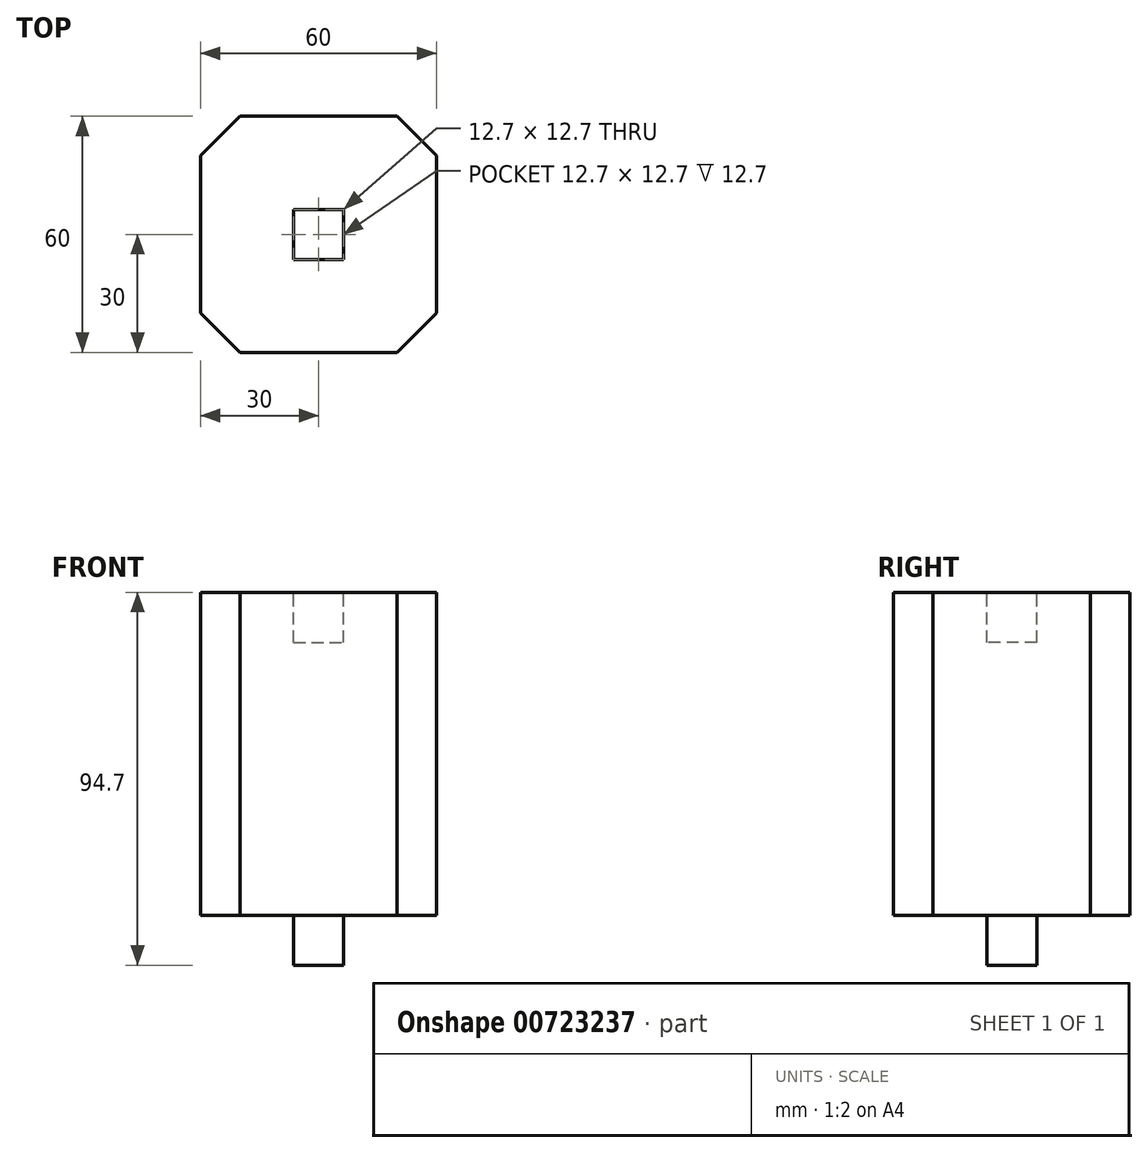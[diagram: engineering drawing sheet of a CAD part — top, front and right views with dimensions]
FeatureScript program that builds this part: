
annotation { "Feature Type Name" : "Feature", "Feature Type Description" : "" }
export const myFeature = defineFeature(function(context is Context, id is Id, definition is map)
    precondition{}
    {
        {
            var Q0;
            Q0=qCreatedBy(makeId("Top.planeOp"),FACE);
            var sketch = newSketch(context, id + "F0", { "sketchPlane" : qUnion([Q0])});
            skLineSegment(sketch, "E0.bottom", {"start": v(-30, 30) * mm, "end": v(30, 30) * mm});
            skLineSegment(sketch, "E0.top", {"start": v(-30, -30) * mm, "end": v(30, -30) * mm});
            skLineSegment(sketch, "E0.left", {"start": v(-30, 30) * mm, "end": v(-30, -30) * mm});
            skLineSegment(sketch, "E0.right", {"start": v(30, 30) * mm, "end": v(30, -30) * mm});
            skSolve(sketch);
        }
        {
            var Q0;
            Q0=qSketchRegion(id+"F0",true);
            extrude(context, id + "F1", {"entities" : qUnion([Q0]), "depth" : 82 * mm, "offsetDistance" : 25 * mm});
        }
        {
            var Q0;
            Q0=makeQuery(id+"F1.opExtrude","SWEPT_EDGE",EDGE,{"disambiguationData":[OSD([sQuery(id+"F0.wireOp",EDGE,"E0.top"),sQuery(id+"F0.wireOp",EDGE,"E0.right")])]});
            var Q1;
            Q1=makeQuery(id+"F1.opExtrude","SWEPT_EDGE",EDGE,{"disambiguationData":[OSD([sQuery(id+"F0.wireOp",EDGE,"E0.bottom"),sQuery(id+"F0.wireOp",EDGE,"E0.right")])]});
            var Q2;
            Q2=makeQuery(id+"F1.opExtrude","SWEPT_EDGE",EDGE,{"disambiguationData":[OSD([sQuery(id+"F0.wireOp",EDGE,"E0.top"),sQuery(id+"F0.wireOp",EDGE,"E0.left")])]});
            var Q3;
            Q3=makeQuery(id+"F1.opExtrude","SWEPT_EDGE",EDGE,{"disambiguationData":[OSD([sQuery(id+"F0.wireOp",EDGE,"E0.bottom"),sQuery(id+"F0.wireOp",EDGE,"E0.left")])]});
            chamfer(context, id + "F2", {"entities" : qUnion([Q0, Q1, Q2, Q3]), "width" : 10 * mm, "tangentPropagation" : true});
        }
        {
            var Q0;
            Q0=makeQuery(id+"F1.opExtrude","CAP_FACE",FACE,{"disambiguationData":[OSD([sQuery(id+"F0.wireOp",EDGE,"E0.bottom"),sQuery(id+"F0.wireOp",EDGE,"E0.top"),sQuery(id+"F0.wireOp",EDGE,"E0.left"),sQuery(id+"F0.wireOp",EDGE,"E0.right")])],"isStart":false});
            var sketch = newSketch(context, id + "F3", { "sketchPlane" : qUnion([Q0])});
            skLineSegment(sketch, "E1.bottom", {"start": v(-6.35, 6.35) * mm, "end": v(6.35, 6.35) * mm});
            skLineSegment(sketch, "E1.top", {"start": v(-6.35, -6.35) * mm, "end": v(6.35, -6.35) * mm});
            skLineSegment(sketch, "E1.left", {"start": v(-6.35, 6.35) * mm, "end": v(-6.35, -6.35) * mm});
            skLineSegment(sketch, "E1.right", {"start": v(6.35, 6.35) * mm, "end": v(6.35, -6.35) * mm});
            skSolve(sketch);
        }
        {
            var Q0;
            Q0=qSketchRegion(id+"F3",true);
            extrude(context, id + "F4", {"entities" : qUnion([Q0]), "operationType" : NewBodyOperationType.REMOVE, "oppositeDirection" : true, "depth" : 12.7 * mm, "offsetDistance" : 25 * mm});
        }
        {
            var Q0;
            Q0=makeQuery(id+"F1.opExtrude","CAP_FACE",FACE,{"disambiguationData":[OSD([sQuery(id+"F0.wireOp",EDGE,"E0.bottom"),sQuery(id+"F0.wireOp",EDGE,"E0.top"),sQuery(id+"F0.wireOp",EDGE,"E0.left"),sQuery(id+"F0.wireOp",EDGE,"E0.right")])],"isStart":true});
            var sketch = newSketch(context, id + "F5", { "sketchPlane" : qUnion([Q0])});
            skLineSegment(sketch, "E2.bottom", {"start": v(-6.35, 6.35) * mm, "end": v(6.35, 6.35) * mm});
            skLineSegment(sketch, "E2.top", {"start": v(-6.35, -6.35) * mm, "end": v(6.35, -6.35) * mm});
            skLineSegment(sketch, "E2.left", {"start": v(-6.35, 6.35) * mm, "end": v(-6.35, -6.35) * mm});
            skLineSegment(sketch, "E2.right", {"start": v(6.35, 6.35) * mm, "end": v(6.35, -6.35) * mm});
            skSolve(sketch);
        }
        {
            var Q0;
            Q0=qSketchRegion(id+"F5",true);
            extrude(context, id + "F6", {"entities" : qUnion([Q0]), "operationType" : NewBodyOperationType.ADD, "depth" : 12.7 * mm, "offsetDistance" : 25 * mm});
        }
    });
